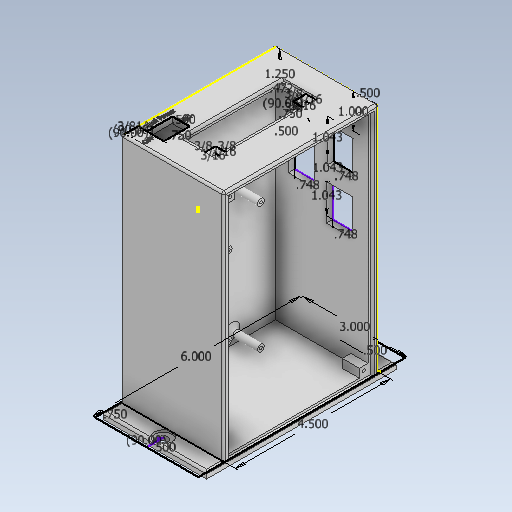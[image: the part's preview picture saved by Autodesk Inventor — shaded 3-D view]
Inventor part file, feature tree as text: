
AUTODESK INVENTOR PART (.ipt)
format: ipt  version: 2020 (Build 240168000, 168)  size: 4,416,000 bytes
history: native  units: in
note: dims shown in document units (in); Inventor stores cm internally (conversion verified against a paired STEP export)
features: sketch x24, extrude x17, hole x5, fillet x3, revolve x3, helix x3, thread x2, pattern_linear x2, other x1
ambient origin geometry x8: Origin, YZ Plane, XZ Plane, XY Plane, X Axis, Y Axis, Z Axis, Center Point
bodies: Solid1 (feature_tree), Solid3 (feature_tree), Solid4 (feature_tree), Solid5 (feature_tree)
feature tree (60):
  sketch  "Sketch1"  dims[d0=3.0in d1=6.0in]
  extrude  "Extrusion1"  Depth=6.0in
  extrude  "Extrusion2"  Depth=4.5in
  hole  "Hole1"  [1 undecoded]
  extrude  "Extrusion7"  Depth=0.1875in
  extrude  "Extrusion8"  Depth=0.1875in
  extrude  "Extrusion3"  Depth=0.125in
  extrude  "Extrusion4"  Depth=0.125in
  extrude  "Extrusion5"  Depth=0.125in TaperAngle=0.0deg
  extrude  "Extrusion6"  Depth=0.25in
  extrude  "Extrusion9"  Depth=0.5in
  hole  "Hole2"  [1 undecoded]
  thread  "Thread1"  [1 undecoded]
  pattern_linear  "Rectangular Pattern1"  Count1=2 Spacing1=1.9291in
  extrude  "Extrusion10"  Depth=0.3937in
  sketch  "Sketch13"  dims[d32=0.25in d33=0.25in d34=0.0in d35=0.5906in]
  hole  "Hole5"  [1 undecoded]
  thread  "Thread3"  [1 undecoded]
  pattern_linear  "Rectangular Pattern2"  Spacing1=0.1875in  [1 undecoded]
  hole  "Hole4"  [1 undecoded]
  fillet  "Fillet1"  Radius=0.125in
  extrude  "Extrusion11"  Depth=0.125in
  extrude  "Extrusion12"  Depth=0.3937in
  sketch  "Sketch18"  dims[d38=2.2835in]
  extrude  "Extrusion13"  Depth=0.3937in
  hole  "Hole6"  [1 undecoded]
  fillet  "Fillet2"  Radius=0.841in
  other  "iFeature13:2"
  sketch  "Sketch20"  dims[d41=0.5in]
  extrude  "Extrusion14"  Depth=0.3937in
  extrude  "Extrusion15"  Depth=0.3937in
  sketch  "Sketch21"  dims[d42=90.0deg]
  extrude  "Extrusion16"  TaperAngle=0.0deg  [1 undecoded]
  extrude  "Extrusion17"  Depth=0.3937in
  fillet  "Fillet3"  Radius=3.0in
  revolve  "Revolution2"  [1 undecoded]
  helix  "Coil2"  [1 undecoded]
  revolve  "Revolution3"  [1 undecoded]
  helix  "Coil3"  [1 undecoded]
  revolve  "Revolution4"  [1 undecoded]
  helix  "Coil4"  [1 undecoded]
  sketch  "Sketch2"  dims[d2=0.75in d3=4.5in]
  sketch  "Sketch3"  dims[d4=0.1875in d5=0.0in d6=6.75in d7=0.0in]
  sketch  "Sketch4"  dims[d8=0.5in]
  sketch  "Sketch5"  dims[d9=0.266in d10=0.75in d11=0.507in d12=0.0625in d13=0.5635in d14=1.0in d15=0.8108in d16=0.1875in]
  sketch  "Sketch6"  dims[d17=0.1875in d18=0.1875in]
  sketch  "Sketch7"  dims[d19=2.8125in d20=0.0in d21=0.125in]
  sketch  "Sketch8"  dims[d22=0.125in d23=0.125in]
  sketch  "Sketch9"  dims[d24=0.125in d25=0.125in d26=0.0in]
  sketch  "Sketch10"  dims[d27=0.5in d28=0.25in]
  sketch  "Sketch12"  dims[d29=0.25in d30=0.0in d31=0.5in]
  sketch  "Sketch16"  dims[d36=0.3937in]
  sketch  "Sketch17"  dims[d37=1.9291in]
  sketch  "Sketch19"  dims[d39=0.25in d40=0.0in]
  sketch  "Sketch24"  dims[d43=0.25in d44=0.0in]
  sketch  "Sketch25"  dims[d45=0.1969in]
  sketch  "Sketch26"  dims[d46=0.25in d47=0.0in]
  sketch  "Sketch27"  dims[d48=0.0807in d49=0.197in d50=0.119in d51=0.188in d52=90.0deg d53=0.25in d54=0.8108in]
  sketch  "Sketch28"  dims[d55=0.25in d56=0.0in d57=0.7874in d59=1.9291in]
  sketch  "Sketch29"  dims[d60=0.7874in d62=2.2835in d63=0.4035in d65=0.8406in d66=0.0in d76=0.7874in d78=2.6772in d79=0.7874in d81=3.6614in d82=0.1875in d83=0.1875in d84=0.125in d85=0.125in d86=0.089in d87=0.146in d88=0.119in d89=0.188in d90=0.5635in d91=0.224in d92=0.8108in d93=0.0625in d94=0.0492in d95=0.1969in d96=0.0807in d97=0.197in d98=0.119in d99=0.188in d100=0.5635in d101=0.259in d102=0.8108in d103=0.841in d104=0.0in d128=2.75in d130=1.5in d131=0.0in d132=1.0in d133=3.0in d134=0.0625in d135=0.0in d136=1.5in d137=0.5in d138=90.0deg d139=0.75in d140=2.75in d141=0.125in d142=0.0in d143=0.375in d144=0.375in d145=0.375in d146=0.375in d147=0.375in d148=0.0in d149=0.1875in d150=0.1875in d151=0.1875in d152=0.1875in d153=0.089in d154=0.197in d155=0.119in d156=0.188in d157=0.5635in d158=0.259in d159=0.8108in d160=0.0625in d161=0.12in d163=0.492in d165=0.129in d167=0.04in d173=1.25in d174=0.75in d175=90.0deg d176=0.4724in d177=0.375in d178=0.0in d179=0.5in d180=1.0in d181=0.748in d182=1.043in d183=0.5in d184=0.748in d185=1.043in d186=0.0197in d187=0.0in d188=0.375in d189=90.0deg d190=0.25in d191=90.0deg d192=0.5in d193=0.75in d194=0.25in d195=0.0in d196=0.0197in d197=0.0in d198=0.125in d206=0.3779in d217=0.3779in d218=0.0028in d219=0.0028in d222=0.0177in d224=0.3779in d226=0.0in d227=0.0177in d228=0.2854in d229=0.3937in d230=0.0in d231=0.0in d232=0.0in d233=0.0in d234=0.0in d235=0.748in d236=1.043in d237=0.3779in d238=0.0028in d239=0.0028in d242=0.0177in d244=0.3779in d246=0.0in d247=0.0177in d248=0.2854in d249=0.3937in d250=0.0in d251=0.0in d252=0.0in d253=0.0in d254=0.0in d255=0.3779in d256=0.0028in d257=0.0028in d260=0.0177in d262=0.3779in d264=0.0in d265=0.0177in d266=0.876in d267=0.3937in d268=0.0in d269=0.0in d270=0.0in d271=0.0in d272=0.0in]
note: 15 required parameter values undecoded (feature->parameter linkage not recoverable at this tier; creation-order binding heuristic only, values carry confidence <= 0.55)